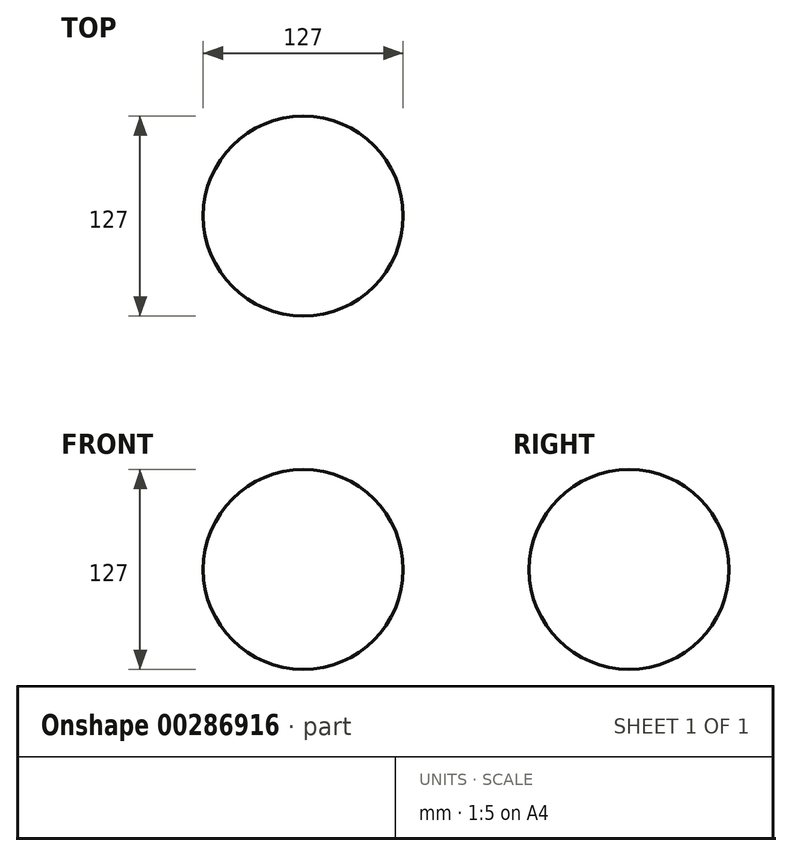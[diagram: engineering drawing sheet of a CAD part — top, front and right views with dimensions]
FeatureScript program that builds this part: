
annotation { "Feature Type Name" : "Feature", "Feature Type Description" : "" }
export const myFeature = defineFeature(function(context is Context, id is Id, definition is map)
    precondition{}
    {
        {
            var Q0;
            Q0=qCreatedBy(makeId("Front.planeOp"),FACE);
            var sketch = newSketch(context, id + "F0", { "sketchPlane" : qUnion([Q0])});
            skArc(sketch, "E0", {"start": v(0, 63.5) * mm, "mid": v(-63.5, 0) * mm, "end": v(0, -63.5) * mm});
            skLineSegment(sketch, "E1", {"start": v(0, 63.5) * mm, "end": v(0, -63.5) * mm});
            skSolve(sketch);
        }
        {
            var Q0;
            Q0 = qSketchRegion(id + "F0", true);
            var Q1;
            Q1=sQuery(id+"F0.wireOp",EDGE,"E1");
            revolve(context, id + "F1", {"entities" : qUnion([Q0]), "axis" : qUnion([Q1]), "revolveType" : RevolveType.FULL});
        }
    });
